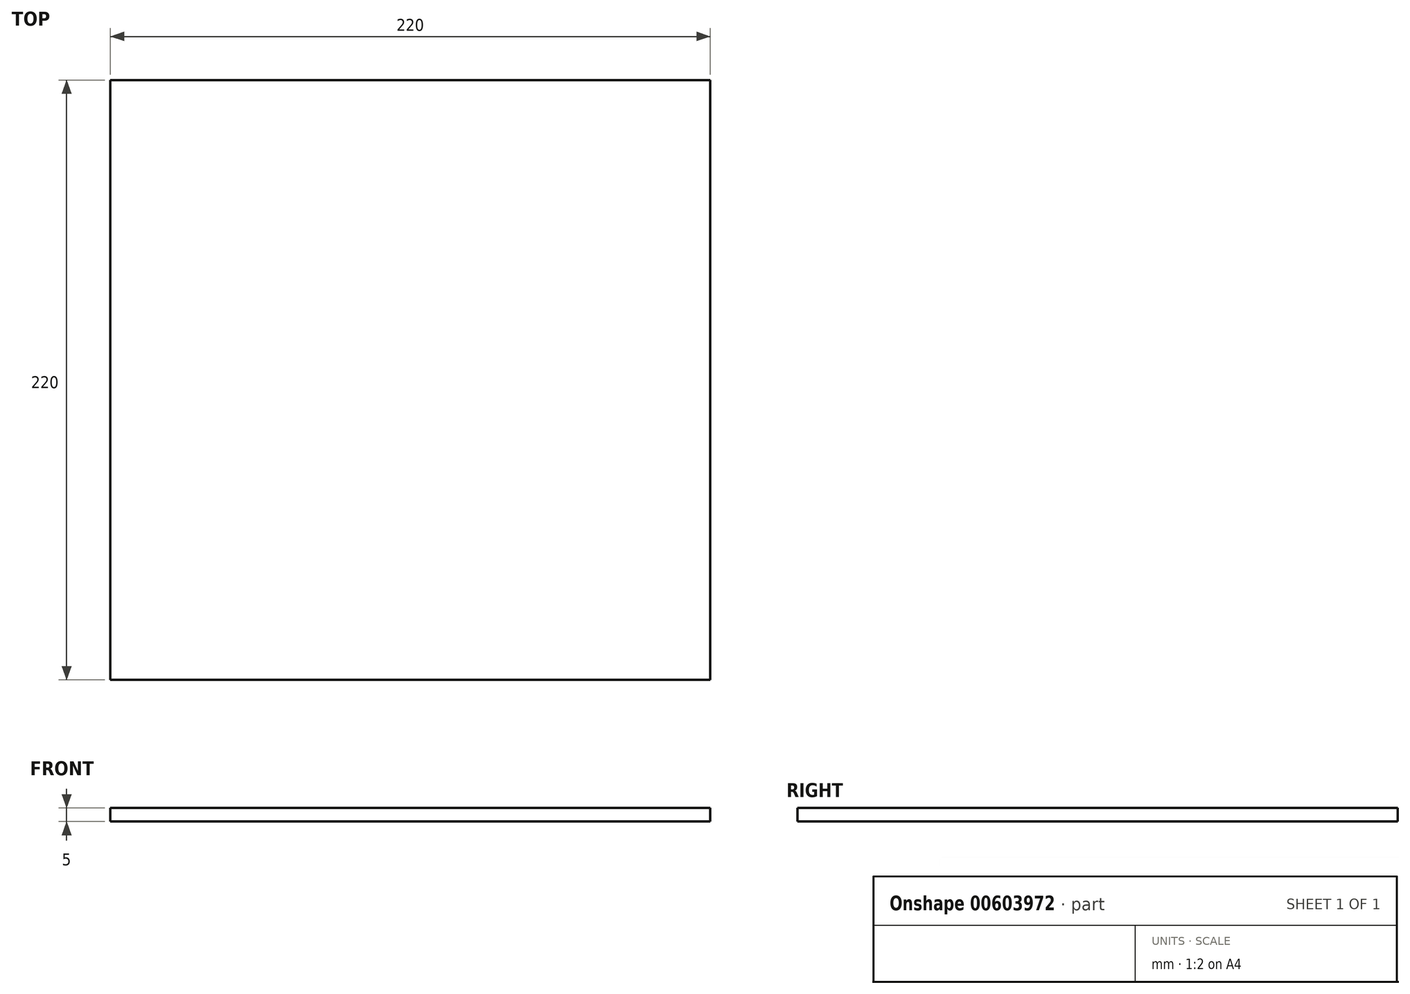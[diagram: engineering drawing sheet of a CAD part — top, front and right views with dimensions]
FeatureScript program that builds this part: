
annotation { "Feature Type Name" : "Feature", "Feature Type Description" : "" }
export const myFeature = defineFeature(function(context is Context, id is Id, definition is map)
    precondition{}
    {
        {
            var Q0;
            Q0=qCreatedBy(makeId("Top.planeOp"),FACE);
            var sketch = newSketch(context, id + "F0", { "sketchPlane" : qUnion([Q0])});
            skLineSegment(sketch, "E0.bottom", {"start": v(-110, 110) * mm, "end": v(110, 110) * mm});
            skLineSegment(sketch, "E0.top", {"start": v(-110, -110) * mm, "end": v(110, -110) * mm});
            skLineSegment(sketch, "E0.left", {"start": v(-110, 110) * mm, "end": v(-110, -110) * mm});
            skLineSegment(sketch, "E0.right", {"start": v(110, 110) * mm, "end": v(110, -110) * mm});
            skPoint(sketch, "E0.middle", {"position": v(0, 0) * mm});
            skSolve(sketch);
        }
        {
            var Q0;
            Q0=makeQuery(id+"F0.imprint","IMPRINT",FACE,{"disambiguationData":[TD([[makeQuery(id+"F0.imprint","IMPRINT",EDGE,{"derivedFrom":sQuery(id+"F0.wireOp",EDGE,"E0.bottom")}),-1.0]])]});
            var Q1;
            Q1 = qSketchRegion(id + "F0", true);
            extrude(context, id + "F1", {"entities" : qUnion([Q0, Q1]), "depth" : 5 * mm, "offsetDistance" : 25 * mm});
        }
    });
